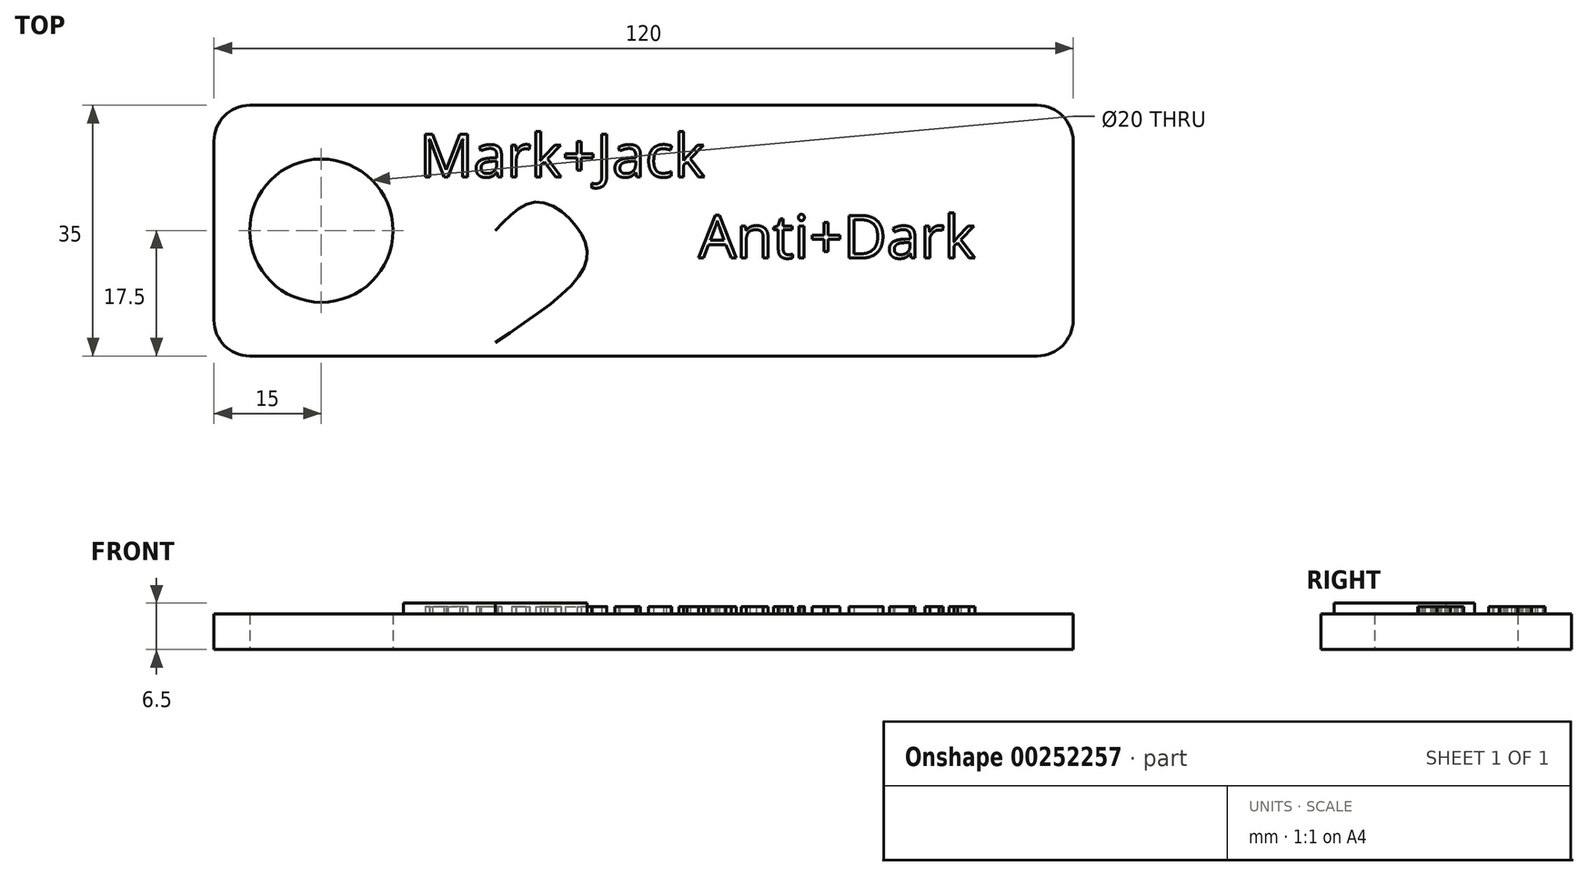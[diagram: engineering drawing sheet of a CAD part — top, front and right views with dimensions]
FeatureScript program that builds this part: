
annotation { "Feature Type Name" : "Feature", "Feature Type Description" : "" }
export const myFeature = defineFeature(function(context is Context, id is Id, definition is map)
    precondition{}
    {
        {
            var Q0;
            Q0=qCreatedBy(makeId("Top.planeOp"),FACE);
            var sketch = newSketch(context, id + "F0", { "sketchPlane" : qUnion([Q0])});
            skPoint(sketch, "E0.middle", {"position": v(0, 0) * mm});
            skLineSegment(sketch, "E1.bottom", {"start": v(60, -17.5) * mm, "end": v(-60, -17.5) * mm});
            skLineSegment(sketch, "E1.top", {"start": v(60, 17.5) * mm, "end": v(-60, 17.5) * mm});
            skLineSegment(sketch, "E1.left", {"start": v(60, -17.5) * mm, "end": v(60, 17.5) * mm});
            skLineSegment(sketch, "E1.right", {"start": v(-60, -17.5) * mm, "end": v(-60, 17.5) * mm});
            skCircle(sketch, "E2", {"center": v(-45, 0) * mm, "radius": 10 * mm});
            skSolve(sketch);
        }
        {
            var Q0;
            Q0=makeQuery(id+"F0.imprint","IMPRINT",FACE,{"disambiguationData":[TD([[makeQuery(id+"F0.imprint","IMPRINT",EDGE,{"derivedFrom":sQuery(id+"F0.wireOp",EDGE,"E1.bottom")}),-1.0]])]});
            extrude(context, id + "F1", {"entities" : qUnion([Q0]), "depth" : 5 * mm});
        }
        {
            var Q0;
            Q0=makeQuery(id+"F1.opExtrude","SWEPT_EDGE",EDGE,{"disambiguationData":[OSD([sQuery(id+"F0.wireOp",EDGE,"E1.bottom"),sQuery(id+"F0.wireOp",EDGE,"E1.left")])]});
            fillet(context, id + "F2", {"entities" : qUnion([Q0]), "radius" : 5 * mm, "tangentPropagation" : true, "allowEdgeOverflow" : false});
        }
        {
            var Q0;
            Q0=makeQuery(id+"F1.opExtrude","SWEPT_EDGE",EDGE,{"disambiguationData":[OSD([sQuery(id+"F0.wireOp",EDGE,"E1.top"),sQuery(id+"F0.wireOp",EDGE,"E1.left")])]});
            fillet(context, id + "F3", {"entities" : qUnion([Q0]), "radius" : 5 * mm, "tangentPropagation" : true, "allowEdgeOverflow" : false});
        }
        {
            var Q0;
            Q0=makeQuery(id+"F1.opExtrude","SWEPT_EDGE",EDGE,{"disambiguationData":[OSD([sQuery(id+"F0.wireOp",EDGE,"E1.top"),sQuery(id+"F0.wireOp",EDGE,"E1.right")])]});
            fillet(context, id + "F4", {"entities" : qUnion([Q0]), "radius" : 5 * mm, "tangentPropagation" : true, "allowEdgeOverflow" : false});
        }
        {
            var Q0;
            Q0=makeQuery(id+"F1.opExtrude","SWEPT_EDGE",EDGE,{"disambiguationData":[OSD([sQuery(id+"F0.wireOp",EDGE,"E1.bottom"),sQuery(id+"F0.wireOp",EDGE,"E1.right")])]});
            fillet(context, id + "F5", {"entities" : qUnion([Q0]), "radius" : 5 * mm, "tangentPropagation" : true, "allowEdgeOverflow" : false});
        }
        {
            var Q0;
            Q0=qCreatedBy(makeId("Top.planeOp"),FACE);
            var sketch = newSketch(context, id + "F6", { "sketchPlane" : qUnion([Q0])});
            skText(sketch, "E3", { "text": "Mark+Jack\n                  Anti+Dark", "fontName": "OpenSans-Regular.ttf"});
            const initialGuessF6  = {"E3": [-0.03131, 0.0075, 1, 0, 0.006]};
            skSetInitialGuess(sketch, initialGuessF6);
            skSolve(sketch);
        }
        {
            var Q0;
            Q0 = qSketchRegion(id + "F6", true);
            extrude(context, id + "F7", {"entities" : qUnion([Q0]), "operationType" : NewBodyOperationType.ADD, "depth" : 6 * mm});
        }
        {
            var Q0;
            {var subQ0=sQuery(id+"F0.wireOp",EDGE,"E1.right");var subQ1=sQuery(id+"F0.wireOp",EDGE,"E1.top");var subQ2=sQuery(id+"F0.wireOp",EDGE,"E1.left");var subQ3=sQuery(id+"F0.wireOp",EDGE,"E1.bottom");var subQ4=sQuery(id+"F0.wireOp",EDGE,"E2");Q0=makeQuery(id+"F7.boolean.opBoolean","SPLIT",FACE,{"disambiguationData":[TD([makeQuery(id+"F1.opExtrude","SWEPT_FACE",FACE,{"disambiguationData":[OSD([subQ3])]})])],"derivedFrom":makeQuery(id+"F1.opExtrude","CAP_FACE",FACE,{"disambiguationData":[OSD([subQ3,subQ1,subQ2,subQ0,subQ4])],"isStart":false})});}
            var sketch = newSketch(context, id + "F8", { "sketchPlane" : qUnion([Q0])});
            skLineSegment(sketch, "E4", {"start": v(-20.7, 0) * mm, "end": v(-20.7, -15.6) * mm, "construction": true});
            skFitSpline(sketch, "E5", {"points": [v(-20.7, 0) * mm, v(-26.57, 4.02) * mm, v(-32.44, 0) * mm, v(-33.01, -5.3) * mm, v(-20.7, -15.6) * mm], "startDerivative": vector(-24.47, 26.37) * mm, "endDerivative": vector(46.8, -31.04) * mm});
            skFitSpline(sketch, "E6.MirrorCS", {"points": [v(-20.7, 0) * mm, v(-14.82, 4.02) * mm, v(-8.94, 0) * mm, v(-8.37, -5.3) * mm, v(-20.7, -15.6) * mm], "startDerivative": vector(24.47, 26.37) * mm, "endDerivative": vector(-46.8, -31.04) * mm});
            skSolve(sketch);
        }
        {
            var Q0;
            Q0=makeQuery(id+"F8.imprint","IMPRINT",FACE,{"disambiguationData":[TD([[makeQuery(id+"F8.imprint","IMPRINT",EDGE,{"derivedFrom":sQuery(id+"F8.wireOp",EDGE,"E5")}),1.0]])]});
            extrude(context, id + "F9", {"entities" : qUnion([Q0]), "operationType" : NewBodyOperationType.ADD, "depth" : 1.5 * mm});
        }
    });
